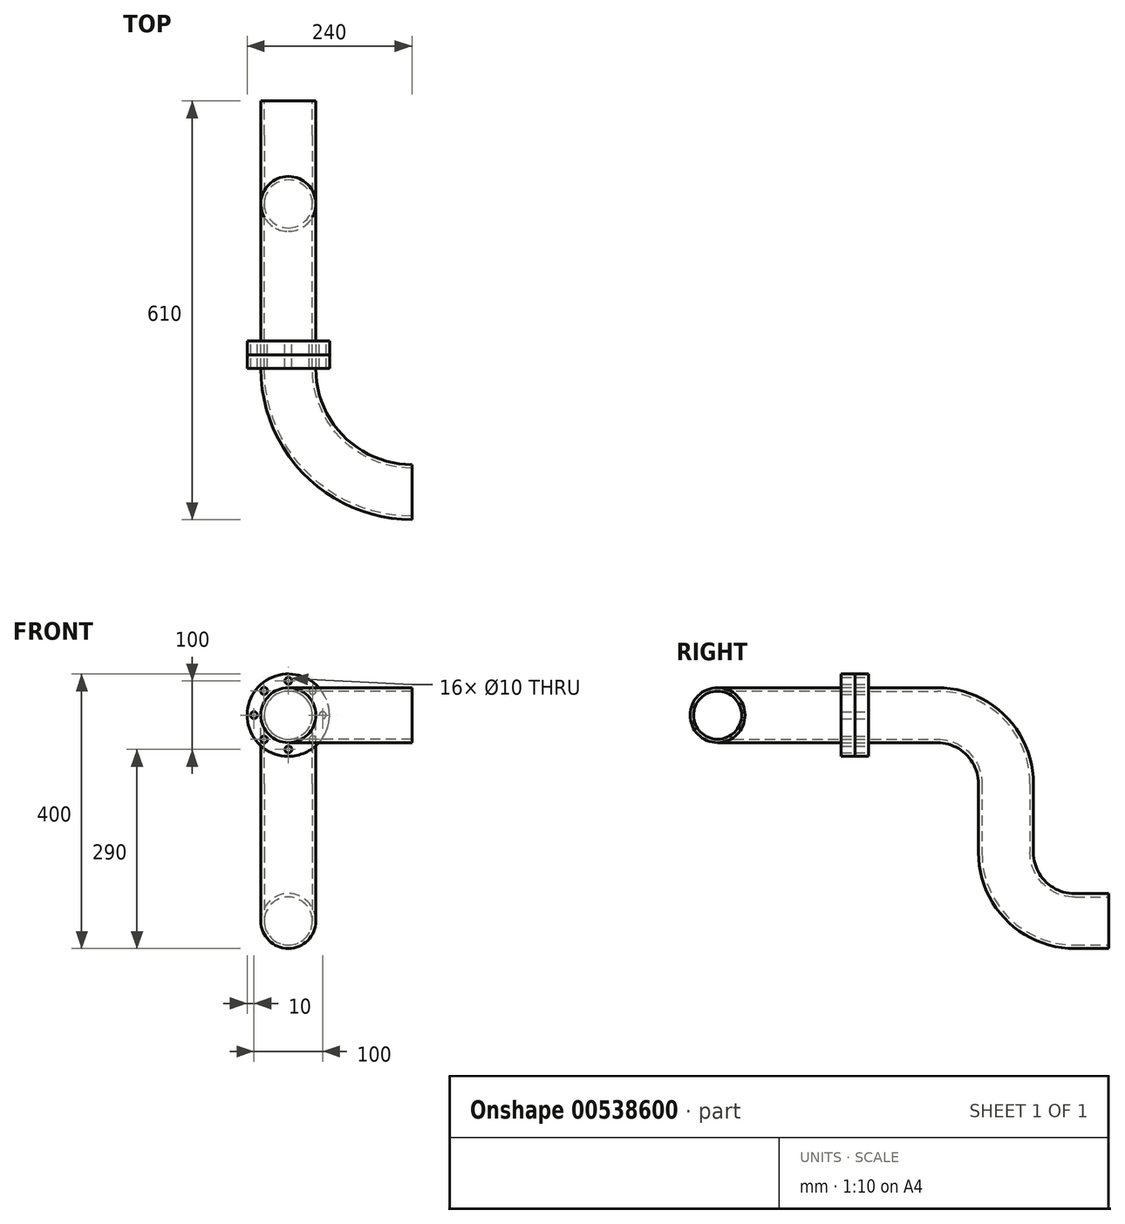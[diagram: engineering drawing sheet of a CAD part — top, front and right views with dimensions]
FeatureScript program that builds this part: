
annotation { "Feature Type Name" : "Feature", "Feature Type Description" : "" }
export const myFeature = defineFeature(function(context is Context, id is Id, definition is map)
    precondition{}
    {
        {
            var Q0;
            Q0=qCreatedBy(makeId("Front.planeOp"),FACE);
            var sketch = newSketch(context, id + "F0", { "sketchPlane" : qUnion([Q0])});
            skCircle(sketch, "E0", {"center": v(0, 0) * mm, "radius": 60 * mm});
            skCircle(sketch, "E1", {"center": v(0, 50) * mm, "radius": 5 * mm});
            skCircle(sketch, "E2.1.0", {"center": v(-35.36, 35.36) * mm, "radius": 5 * mm});
            skCircle(sketch, "E2.2.0", {"center": v(-50, 0) * mm, "radius": 5 * mm});
            skCircle(sketch, "E3.1.3.0", {"center": v(-35.36, -35.36) * mm, "radius": 5 * mm});
            skCircle(sketch, "E3.1.4.0", {"center": v(0, -50) * mm, "radius": 5 * mm});
            skCircle(sketch, "E3.1.5.0", {"center": v(35.36, -35.36) * mm, "radius": 5 * mm});
            skCircle(sketch, "E3.1.6.0", {"center": v(50, 0) * mm, "radius": 5 * mm});
            skCircle(sketch, "E3.1.7.0", {"center": v(35.36, 35.36) * mm, "radius": 5 * mm});
            skCircle(sketch, "E4", {"center": v(0, 0) * mm, "radius": 35 * mm});
            skSolve(sketch);
        }
        {
            var Q0;
            Q0=makeQuery(id+"F0.imprint","IMPRINT",FACE,{"disambiguationData":[TD([[makeQuery(id+"F0.imprint","IMPRINT",EDGE,{"derivedFrom":sQuery(id+"F0.wireOp",EDGE,"E0")}),1.0]])]});
            extrude(context, id + "F1", {"entities" : qUnion([Q0]), "depth" : 20 * mm, "offsetDistance" : 25 * mm});
        }
        {
            var Q0;
            Q0=qCreatedBy(makeId("Front.planeOp"),FACE);
            var sketch = newSketch(context, id + "F2", { "sketchPlane" : qUnion([Q0])});
            skCircle(sketch, "E5", {"center": v(0, 0) * mm, "radius": 35 * mm});
            skCircle(sketch, "E6", {"center": v(0, 0) * mm, "radius": 40 * mm});
            skSolve(sketch);
        }
        {
            var Q0;
            Q0=qCreatedBy(makeId("Right.planeOp"),FACE);
            var sketch = newSketch(context, id + "F3", { "sketchPlane" : qUnion([Q0])});
            skLineSegment(sketch, "E7", {"start": v(0, 0) * mm, "end": v(100, 0) * mm});
            skLineSegment(sketch, "E8", {"start": v(200, -100) * mm, "end": v(200, -200) * mm});
            skLineSegment(sketch, "E9", {"start": v(300, -300) * mm, "end": v(350, -300) * mm});
            skPoint(sketch, "E10.visualSharp", {"position": v(200, 0) * mm});
            skArc(sketch, "E10.filletArc", {"start": v(200, -100) * mm, "mid": v(170.71, -29.29) * mm, "end": v(100, 0) * mm});
            skPoint(sketch, "E11.visualSharp", {"position": v(200, -300) * mm});
            skArc(sketch, "E11.filletArc", {"start": v(200, -200) * mm, "mid": v(229.29, -270.71) * mm, "end": v(300, -300) * mm});
            skSolve(sketch);
        }
        {
            var Q0;
            Q0=makeQuery(id+"F2.imprint","IMPRINT",FACE,{"disambiguationData":[TD([[makeQuery(id+"F2.imprint","IMPRINT",EDGE,{"derivedFrom":sQuery(id+"F2.wireOp",EDGE,"E5")}),-1.0]])]});
            var Q1;
            Q1=sQuery(id+"F3.wireOp",EDGE,"E10.filletArc");
            var Q2;
            Q2=sQuery(id+"F3.wireOp",EDGE,"E8");
            var Q3;
            Q3=sQuery(id+"F3.wireOp",EDGE,"E11.filletArc");
            var Q4;
            Q4=sQuery(id+"F3.wireOp",EDGE,"E9");
            var Q5;
            Q5=sQuery(id+"F3.wireOp",EDGE,"E7");
            sweep(context, id + "F4", {"operationType" : NewBodyOperationType.ADD, "profiles" : qUnion([Q0]), "path" : qUnion([Q1, Q2, Q3, Q4, Q5])});
        }
        {
            var Q0;
            Q0=makeQuery(id+"F1.opExtrude","CAP_FACE",FACE,{"disambiguationData":[OSD([sQuery(id+"F0.wireOp",EDGE,"E0"),sQuery(id+"F0.wireOp",EDGE,"E1"),sQuery(id+"F0.wireOp",EDGE,"E2.1.0"),sQuery(id+"F0.wireOp",EDGE,"E2.2.0"),sQuery(id+"F0.wireOp",EDGE,"E3.1.3.0"),sQuery(id+"F0.wireOp",EDGE,"E3.1.4.0"),sQuery(id+"F0.wireOp",EDGE,"E3.1.5.0"),sQuery(id+"F0.wireOp",EDGE,"E3.1.6.0"),sQuery(id+"F0.wireOp",EDGE,"E3.1.7.0"),sQuery(id+"F0.wireOp",EDGE,"E4")])],"isStart":false});
            extrude(context, id + "F5", {"entities" : qUnion([Q0]), "depth" : 20 * mm, "offsetDistance" : 25 * mm});
        }
        {
            var Q0;
            Q0=makeQuery(id+"F5.opExtrude","CAP_FACE",FACE,{"disambiguationData":[OSD([sQuery(id+"F0.wireOp",EDGE,"E0"),sQuery(id+"F0.wireOp",EDGE,"E1"),sQuery(id+"F0.wireOp",EDGE,"E2.1.0"),sQuery(id+"F0.wireOp",EDGE,"E2.2.0"),sQuery(id+"F0.wireOp",EDGE,"E3.1.3.0"),sQuery(id+"F0.wireOp",EDGE,"E3.1.4.0"),sQuery(id+"F0.wireOp",EDGE,"E3.1.5.0"),sQuery(id+"F0.wireOp",EDGE,"E3.1.6.0"),sQuery(id+"F0.wireOp",EDGE,"E3.1.7.0"),sQuery(id+"F0.wireOp",EDGE,"E4")])],"isStart":false});
            var sketch = newSketch(context, id + "F6", { "sketchPlane" : qUnion([Q0])});
            skCircle(sketch, "E12", {"center": v(0, 0) * mm, "radius": 35 * mm});
            skCircle(sketch, "E13", {"center": v(0, 0) * mm, "radius": 40 * mm});
            skCircle(sketch, "E14", {"center": v(0, 50) * mm, "radius": 5 * mm});
            skCircle(sketch, "E15.1.0", {"center": v(-35.36, 35.36) * mm, "radius": 5 * mm});
            skCircle(sketch, "E15.2.0", {"center": v(-50, 0) * mm, "radius": 5 * mm});
            skCircle(sketch, "E16.1.3.0", {"center": v(-35.36, -35.36) * mm, "radius": 5 * mm});
            skCircle(sketch, "E16.1.4.0", {"center": v(0, -50) * mm, "radius": 5 * mm});
            skCircle(sketch, "E16.1.5.0", {"center": v(35.36, -35.36) * mm, "radius": 5 * mm});
            skCircle(sketch, "E16.1.6.0", {"center": v(50, 0) * mm, "radius": 5 * mm});
            skCircle(sketch, "E16.1.7.0", {"center": v(35.36, 35.36) * mm, "radius": 5 * mm});
            skLineSegment(sketch, "E17", {"start": v(0, 0) * mm, "end": v(180, 0) * mm, "construction": true});
            skLineSegment(sketch, "E18", {"start": v(180, 85.46) * mm, "end": v(180, 0) * mm, "construction": true});
            skLineSegment(sketch, "E19", {"start": v(180, 0) * mm, "end": v(180, -72.84) * mm, "construction": true});
            skSolve(sketch);
        }
        {
            var Q0;
            Q0=makeQuery(id+"F6.imprint","IMPRINT",FACE,{"disambiguationData":[TD([[makeQuery(id+"F6.imprint","IMPRINT",EDGE,{"derivedFrom":sQuery(id+"F6.wireOp",EDGE,"E12")}),-1.0]])]});
            var Q1;
            Q1=sQuery(id+"F6.wireOp",EDGE,"E18");
            revolve(context, id + "F7", {"operationType" : NewBodyOperationType.ADD, "entities" : qUnion([Q0]), "axis" : qUnion([Q1]), "revolveType" : RevolveType.ONE_DIRECTION, "oppositeDirection" : true, "angle" : 90 * degree});
        }
    });
